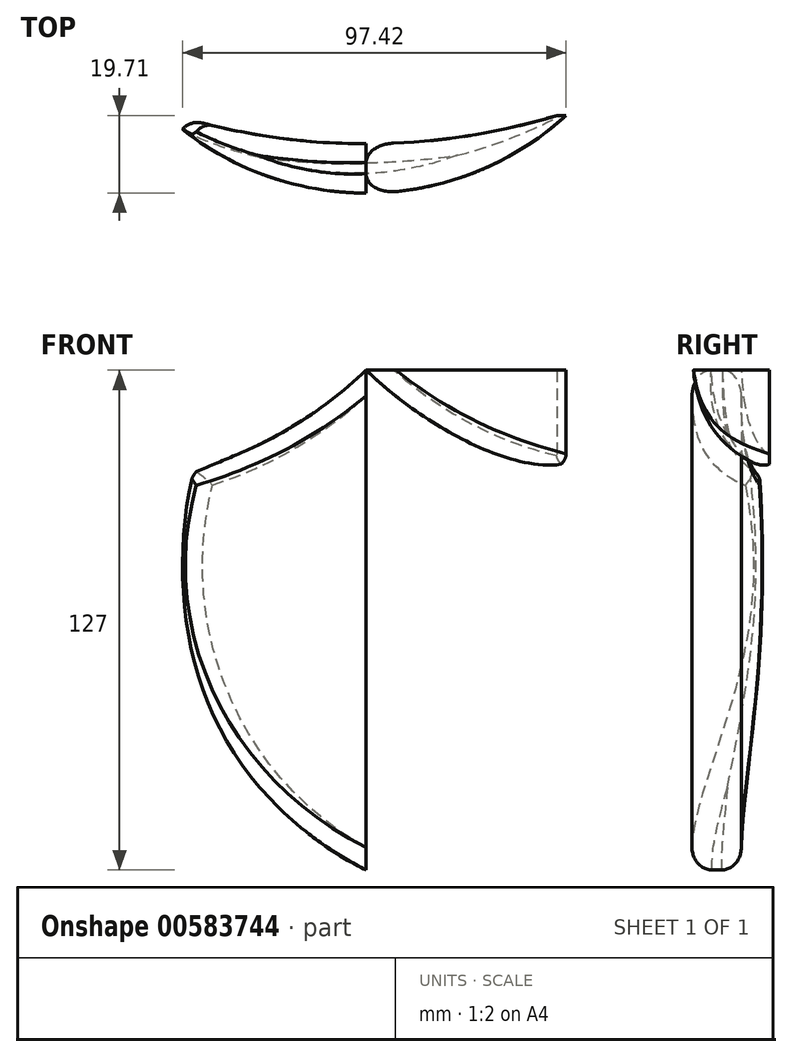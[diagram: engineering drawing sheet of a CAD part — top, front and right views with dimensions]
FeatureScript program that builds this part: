
annotation { "Feature Type Name" : "Feature", "Feature Type Description" : "" }
export const myFeature = defineFeature(function(context is Context, id is Id, definition is map)
    precondition{}
    {
        {
            var Q0;
            Q0=qCreatedBy(makeId("Top.planeOp"),FACE);
            var sketch = newSketch(context, id + "F0", { "sketchPlane" : qUnion([Q0])});
            skArc(sketch, "E0", {"start": v(-50.8, 0) * mm, "mid": v(0, -19.7) * mm, "end": v(50.8, 0) * mm});
            skArc(sketch, "E1", {"start": v(-50.8, 0) * mm, "mid": v(0, -8.2) * mm, "end": v(50.8, 0) * mm});
            skLineSegment(sketch, "E2", {"start": v(0, 0) * mm, "end": v(-50.8, 0) * mm});
            skLineSegment(sketch, "E3", {"start": v(0, 0) * mm, "end": v(50.8, 0) * mm});
            skSolve(sketch);
        }
        {
            var Q0;
            Q0 = qSketchRegion(id + "F0", true);
            extrude(context, id + "F1", {"entities" : qUnion([Q0]), "depth" : 127 * mm, "offsetDistance" : 25.4 * mm});
        }
        {
            var Q0;
            Q0=qCreatedBy(makeId("Front.planeOp"),FACE);
            var sketch = newSketch(context, id + "F2", { "sketchPlane" : qUnion([Q0])});
            skLineSegment(sketch, "E4", {"start": v(0, 0) * mm, "end": v(0, 127) * mm});
            skLineSegment(sketch, "E5", {"start": v(0, 127) * mm, "end": v(-44.45, 127) * mm});
            skLineSegment(sketch, "E6", {"start": v(-44.45, 127) * mm, "end": v(-44.45, 101.6) * mm});
            skArc(sketch, "E7", {"start": v(-44.45, 101.6) * mm, "mid": v(-40.67, 42.73) * mm, "end": v(0, 0) * mm});
            skArc(sketch, "E8", {"start": v(-44.45, 101.6) * mm, "mid": v(-20.65, 111.55) * mm, "end": v(0, 127) * mm});
            skArc(sketch, "E9.MirrorCS", {"start": v(44.45, 101.6) * mm, "mid": v(20.65, 111.55) * mm, "end": v(0, 127) * mm});
            skArc(sketch, "E10.MirrorCS", {"start": v(44.45, 101.6) * mm, "mid": v(40.67, 42.73) * mm, "end": v(0, 0) * mm});
            skLineSegment(sketch, "E11", {"start": v(0, 127) * mm, "end": v(-65.82, 127) * mm});
            skLineSegment(sketch, "E12", {"start": v(-65.82, 127) * mm, "end": v(-65.82, 0) * mm});
            skLineSegment(sketch, "E13", {"start": v(-65.82, 0) * mm, "end": v(70.03, 0) * mm});
            skLineSegment(sketch, "E14", {"start": v(70.03, 0) * mm, "end": v(70.03, 127) * mm});
            skLineSegment(sketch, "E15", {"start": v(70.03, 127) * mm, "end": v(0, 127) * mm});
            skSolve(sketch);
        }
        {
            var Q0;
            Q0=makeQuery(id+"F2.imprint","IMPRINT",FACE,{"disambiguationData":[TD([[makeQuery(id+"F2.imprint","IMPRINT",EDGE,{"derivedFrom":sQuery(id+"F2.wireOp",EDGE,"E9.MirrorCS")}),-1.0]])]});
            var Q1;
            {var subQ0=sQuery(id+"F2.wireOp",EDGE,"E6");Q1=makeQuery(id+"F2.imprint","IMPRINT",FACE,{"disambiguationData":[TD([[makeQuery(id+"F2.imprint","IMPRINT",EDGE,{"derivedFrom":subQ0}),1.0]])]});}
            var Q2;
            {var subQ2=sQuery(id+"F2.wireOp",EDGE,"E6");Q2=makeQuery(id+"F2.imprint","IMPRINT",FACE,{"disambiguationData":[TD([[makeQuery(id+"F2.imprint","IMPRINT",EDGE,{"derivedFrom":subQ2}),-1.0]])]});}
            extrude(context, id + "F3", {"entities" : qUnion([Q0, Q1, Q2]), "operationType" : NewBodyOperationType.REMOVE, "depth" : 64.77 * mm, "offsetDistance" : 25.4 * mm});
        }
        {
            var Q0;
            Q0=qCreatedBy(makeId("Top.planeOp"),FACE);
            var sketch = newSketch(context, id + "F4", { "sketchPlane" : qUnion([Q0])});
            skArc(sketch, "E16", {"start": v(-48.4, 0) * mm, "mid": v(0.02, -7.19) * mm, "end": v(48.45, 0) * mm});
            skLineSegment(sketch, "E17", {"start": v(-48.4, 0) * mm, "end": v(48.45, 0) * mm});
            skSolve(sketch);
        }
        {
            var Q0;
            Q0 = qSketchRegion(id + "F4", true);
            extrude(context, id + "F5", {"entities" : qUnion([Q0]), "operationType" : NewBodyOperationType.REMOVE, "depth" : 128.27 * mm, "offsetDistance" : 25.4 * mm});
        }
        {
            var Q0;
            Q0=makeQuery(id+"F5.boolean.opBoolean","INTERSECT",EDGE,{"derivedFrom":[makeQuery(id+"F3.boolean.opBoolean","COPY",FACE,{"derivedFrom":makeQuery(id+"F3.opExtrude","SWEPT_FACE",FACE,{"disambiguationData":[OSD([sQuery(id+"F2.wireOp",EDGE,"E10.MirrorCS")])]})}),makeQuery(id+"F5.opExtrude","SWEPT_FACE",FACE,{"disambiguationData":[OSD([sQuery(id+"F4.wireOp",EDGE,"E16")])]})]});
            var Q1;
            Q1=makeQuery(id+"F5.boolean.opBoolean","INTERSECT",EDGE,{"derivedFrom":[makeQuery(id+"F3.boolean.opBoolean","COPY",FACE,{"derivedFrom":makeQuery(id+"F3.opExtrude","SWEPT_FACE",FACE,{"disambiguationData":[OSD([sQuery(id+"F2.wireOp",EDGE,"E7")])]})}),makeQuery(id+"F5.opExtrude","SWEPT_FACE",FACE,{"disambiguationData":[OSD([sQuery(id+"F4.wireOp",EDGE,"E16")])]})]});
            var Q2;
            Q2=makeQuery(id+"F3.boolean.opBoolean","INTERSECT",EDGE,{"derivedFrom":[makeQuery(id+"F1.opExtrude","SWEPT_FACE",FACE,{"disambiguationData":[OSD([sQuery(id+"F0.wireOp",EDGE,"E0")])]}),makeQuery(id+"F3.opExtrude","SWEPT_FACE",FACE,{"disambiguationData":[OSD([sQuery(id+"F2.wireOp",EDGE,"E10.MirrorCS")])]})]});
            var Q3;
            Q3=makeQuery(id+"F3.boolean.opBoolean","INTERSECT",EDGE,{"derivedFrom":[makeQuery(id+"F1.opExtrude","SWEPT_FACE",FACE,{"disambiguationData":[OSD([sQuery(id+"F0.wireOp",EDGE,"E0")])]}),makeQuery(id+"F3.opExtrude","SWEPT_FACE",FACE,{"disambiguationData":[OSD([sQuery(id+"F2.wireOp",EDGE,"E7")])]})]});
            fillet(context, id + "F6", {"entities" : qUnion([Q0, Q1, Q2, Q3]), "radius" : 5.08 * mm, "tangentPropagation" : true, "allowEdgeOverflow" : false});
        }
        {
            var Q0;
            Q0=makeQuery(id+"F5.boolean.opBoolean","INTERSECT",EDGE,{"derivedFrom":[makeQuery(id+"F3.boolean.opBoolean","COPY",FACE,{"derivedFrom":makeQuery(id+"F3.opExtrude","SWEPT_FACE",FACE,{"disambiguationData":[OSD([sQuery(id+"F2.wireOp",EDGE,"E8")])]})}),makeQuery(id+"F5.opExtrude","SWEPT_FACE",FACE,{"disambiguationData":[OSD([sQuery(id+"F4.wireOp",EDGE,"E16")])]})]});
            var Q1;
            Q1=makeQuery(id+"F3.boolean.opBoolean","INTERSECT",EDGE,{"derivedFrom":[makeQuery(id+"F1.opExtrude","SWEPT_FACE",FACE,{"disambiguationData":[OSD([sQuery(id+"F0.wireOp",EDGE,"E0")])]}),makeQuery(id+"F3.opExtrude","SWEPT_FACE",FACE,{"disambiguationData":[OSD([sQuery(id+"F2.wireOp",EDGE,"E8")])]})]});
            var Q2;
            Q2=makeQuery(id+"F3.boolean.opBoolean","INTERSECT",EDGE,{"derivedFrom":[makeQuery(id+"F1.opExtrude","SWEPT_FACE",FACE,{"disambiguationData":[OSD([sQuery(id+"F0.wireOp",EDGE,"E0")])]}),makeQuery(id+"F3.opExtrude","SWEPT_FACE",FACE,{"disambiguationData":[OSD([sQuery(id+"F2.wireOp",EDGE,"E9.MirrorCS")])]})]});
            var Q3;
            Q3=makeQuery(id+"F5.boolean.opBoolean","INTERSECT",EDGE,{"derivedFrom":[makeQuery(id+"F3.boolean.opBoolean","COPY",FACE,{"derivedFrom":makeQuery(id+"F3.opExtrude","SWEPT_FACE",FACE,{"disambiguationData":[OSD([sQuery(id+"F2.wireOp",EDGE,"E9.MirrorCS")])]})}),makeQuery(id+"F5.opExtrude","SWEPT_FACE",FACE,{"disambiguationData":[OSD([sQuery(id+"F4.wireOp",EDGE,"E16")])]})]});
            fillet(context, id + "F7", {"entities" : qUnion([Q0, Q1, Q2, Q3]), "radius" : 4.83 * mm, "tangentPropagation" : true, "allowEdgeOverflow" : false});
        }
        {
            var Q0;
            Q0=qCreatedBy(makeId("Front.planeOp"),FACE);
            cPlane(context, id + "F8", {"entities" : qUnion([Q0]), "cplaneType" : CPlaneType.OFFSET, "offset" : 5.6 * mm, "width" : 152.4 * mm, "height" : 152.4 * mm});
        }
    });
